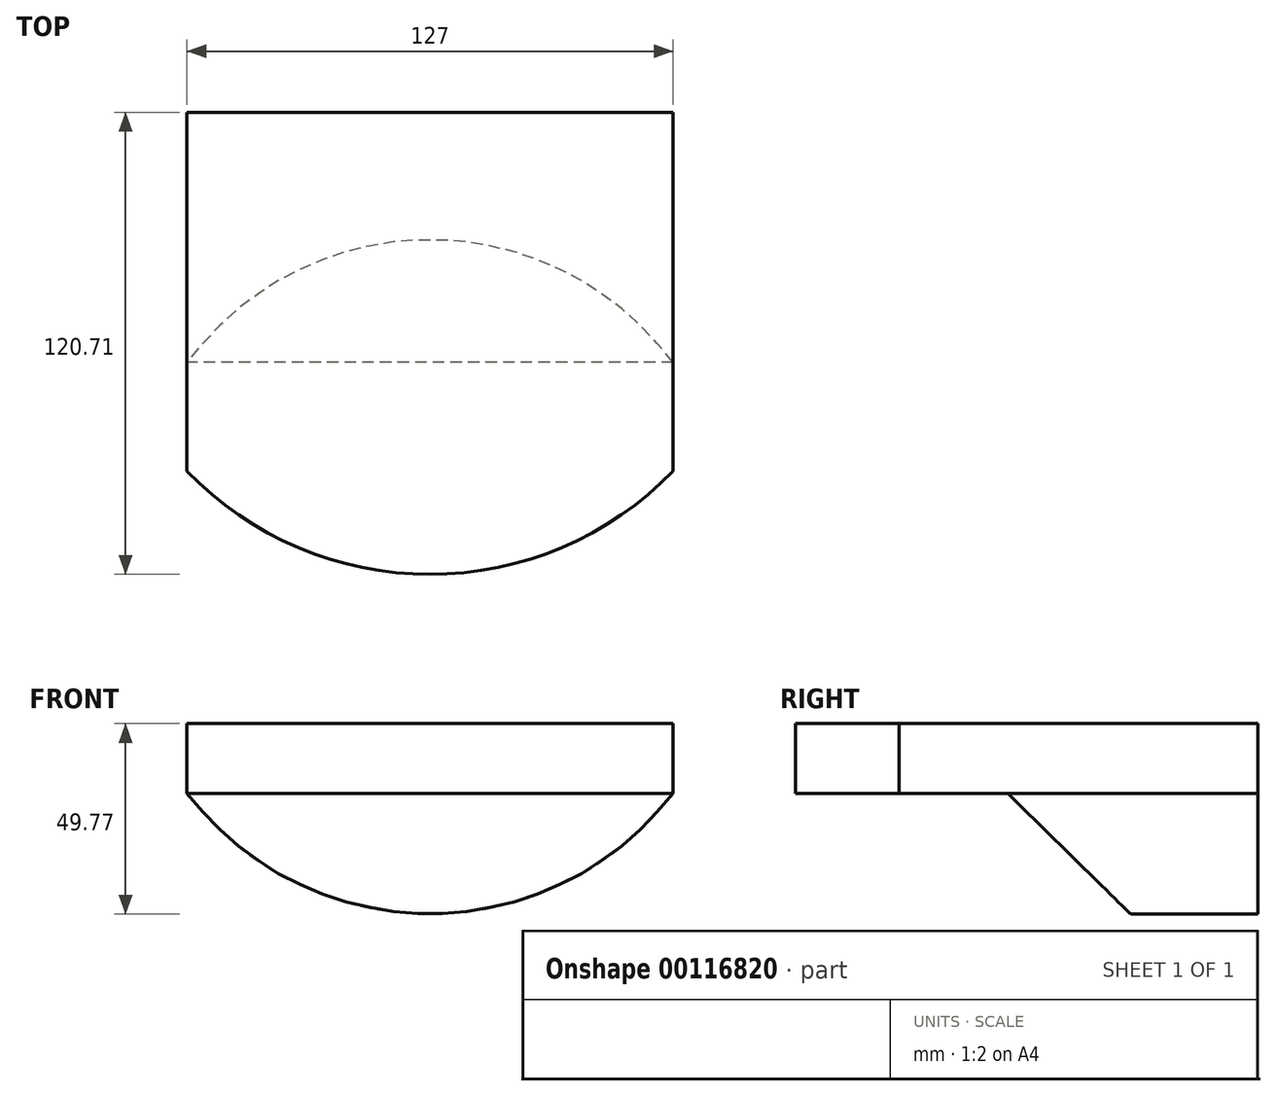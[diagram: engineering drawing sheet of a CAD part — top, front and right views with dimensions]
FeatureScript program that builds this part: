
annotation { "Feature Type Name" : "Feature", "Feature Type Description" : "" }
export const myFeature = defineFeature(function(context is Context, id is Id, definition is map)
    precondition{}
    {
        {
            var Q0;
            Q0=qCreatedBy(makeId("Front.planeOp"),FACE);
            var sketch = newSketch(context, id + "F0", { "sketchPlane" : qUnion([Q0])});
            skLineSegment(sketch, "E0.bottom", {"start": v(-63.5, 31) * mm, "end": v(63.5, 31) * mm});
            skLineSegment(sketch, "E0.top", {"start": v(-63.5, -31) * mm, "end": v(63.5, -31) * mm});
            skLineSegment(sketch, "E0.left", {"start": v(-63.5, 31) * mm, "end": v(-63.5, -31) * mm});
            skLineSegment(sketch, "E0.right", {"start": v(63.5, 31) * mm, "end": v(63.5, -31) * mm});
            skPoint(sketch, "E0.middle", {"position": v(0, 0) * mm});
            skLineSegment(sketch, "E1", {"start": v(0, 0) * mm, "end": v(0, -62.5) * mm});
            skLineSegment(sketch, "E2", {"start": v(0, -62.5) * mm, "end": v(0, 0) * mm});
            skLineSegment(sketch, "E3", {"start": v(0, 0) * mm, "end": v(0, 62.5) * mm});
            skLineSegment(sketch, "E4", {"start": v(0, 62.5) * mm, "end": v(0, 0) * mm});
            skArc(sketch, "E5", {"start": v(63.5, 31) * mm, "mid": v(0, 62.5) * mm, "end": v(-63.5, 31) * mm});
            skArc(sketch, "E6", {"start": v(-63.5, -31) * mm, "mid": v(0, -62.5) * mm, "end": v(63.5, -31) * mm});
            skSolve(sketch);
        }
        {
            var Q0;
            Q0=qSketchRegion(id+"F0",true);
            extrude(context, id + "F1", {"entities" : qUnion([Q0]), "depth" : 104.5 * mm});
        }
        {
            var Q0;
            Q0=makeQuery(id+"F1.opExtrude","SWEPT_FACE",FACE,{"disambiguationData":[OSD([sQuery(id+"F0.wireOp",EDGE,"E0.right")])]});
            var sketch = newSketch(context, id + "F2", { "sketchPlane" : qUnion([Q0])});
            skLineSegment(sketch, "E7.bottom", {"start": v(-104.5, 31) * mm, "end": v(-62.5, 31) * mm});
            skLineSegment(sketch, "E7.top", {"start": v(-104.5, -31) * mm, "end": v(-62.5, -31) * mm});
            skLineSegment(sketch, "E7.left", {"start": v(-104.5, 31) * mm, "end": v(-104.5, -31) * mm});
            skLineSegment(sketch, "E7.right", {"start": v(-62.5, 31) * mm, "end": v(-62.5, -31) * mm});
            skLineSegment(sketch, "E8", {"start": v(-62.5, 31) * mm, "end": v(-62.5, 64.33) * mm});
            skLineSegment(sketch, "E9", {"start": v(-62.5, 64.33) * mm, "end": v(-104.5, 31) * mm});
            skLineSegment(sketch, "E10", {"start": v(-62.5, -31) * mm, "end": v(-62.5, -65.1) * mm});
            skLineSegment(sketch, "E11", {"start": v(-62.5, -65.1) * mm, "end": v(-104.5, -31) * mm});
            skLineSegment(sketch, "E12", {"start": v(-104.5, -31) * mm, "end": v(-104.5, -67.31) * mm});
            skLineSegment(sketch, "E13", {"start": v(-104.5, -67.31) * mm, "end": v(-62.5, -65.1) * mm});
            skLineSegment(sketch, "E14", {"start": v(-104.5, 31) * mm, "end": v(-104.5, 72.84) * mm});
            skLineSegment(sketch, "E15", {"start": v(-104.5, 72.84) * mm, "end": v(-62.5, 64.33) * mm});
            skSolve(sketch);
        }
        {
            var Q0;
            Q0=makeQuery(id+"F2.imprint","IMPRINT",FACE,{"disambiguationData":[TD([[makeQuery(id+"F2.imprint","IMPRINT",EDGE,{"derivedFrom":sQuery(id+"F2.wireOp",EDGE,"E9")}),-1.0]])]});
            var Q1;
            Q1=makeQuery(id+"F2.imprint","IMPRINT",FACE,{"disambiguationData":[TD([[makeQuery(id+"F2.imprint","IMPRINT",EDGE,{"derivedFrom":sQuery(id+"F2.wireOp",EDGE,"E11")}),1.0]])]});
            extrude(context, id + "F3", {"entities" : qUnion([Q0, Q1]), "operationType" : NewBodyOperationType.REMOVE, "endBound" : BoundingType.THROUGH_ALL, "oppositeDirection" : true, "depth" : 25.4 * mm});
        }
        {
            var Q0;
            Q0=makeQuery(id+"F1.opExtrude","CAP_FACE",FACE,{"disambiguationData":[OSD([sQuery(id+"F0.wireOp",EDGE,"E0.left"),sQuery(id+"F0.wireOp",EDGE,"E0.right"),sQuery(id+"F0.wireOp",EDGE,"E5"),sQuery(id+"F0.wireOp",EDGE,"E6")])],"isStart":false});
            var sketch = newSketch(context, id + "F4", { "sketchPlane" : qUnion([Q0])});
            skLineSegment(sketch, "E16.bottom", {"start": v(-63.5, 31) * mm, "end": v(63.5, 31) * mm});
            skLineSegment(sketch, "E16.top", {"start": v(-63.5, -31) * mm, "end": v(63.5, -31) * mm});
            skLineSegment(sketch, "E16.left", {"start": v(-63.5, 31) * mm, "end": v(-63.5, -31) * mm});
            skLineSegment(sketch, "E16.right", {"start": v(63.5, 31) * mm, "end": v(63.5, -31) * mm});
            skSolve(sketch);
        }
        {
            var Q0;
            Q0=qSketchRegion(id+"F4",true);
            extrude(context, id + "F5", {"entities" : qUnion([Q0]), "operationType" : NewBodyOperationType.ADD, "depth" : 27 * mm});
        }
        {
            var Q0;
            Q0=makeQuery(id+"F5.opExtrude","SWEPT_FACE",FACE,{"disambiguationData":[OSD([sQuery(id+"F4.wireOp",EDGE,"E16.top")])]});
            var sketch = newSketch(context, id + "F6", { "sketchPlane" : qUnion([Q0])});
            skPoint(sketch, "E17", {"position": v(0, 131.5) * mm});
            skArc(sketch, "E18", {"start": v(63.5, 104.5) * mm, "mid": v(0, 131.5) * mm, "end": v(-63.5, 104.5) * mm});
            skLineSegment(sketch, "E19.bottom", {"start": v(-63.5, 131.5) * mm, "end": v(63.5, 131.5) * mm});
            skLineSegment(sketch, "E19.top", {"start": v(-63.5, 104.5) * mm, "end": v(63.5, 104.5) * mm});
            skLineSegment(sketch, "E19.left", {"start": v(-63.5, 131.5) * mm, "end": v(-63.5, 104.5) * mm});
            skLineSegment(sketch, "E19.right", {"start": v(63.5, 131.5) * mm, "end": v(63.5, 104.5) * mm});
            skSolve(sketch);
        }
        {
            var Q0;
            {var subQ0=sQuery(id+"F6.wireOp",EDGE,"E19.left");Q0=makeQuery(id+"F6.imprint","IMPRINT",FACE,{"disambiguationData":[TD([[makeQuery(id+"F6.imprint","IMPRINT",EDGE,{"derivedFrom":subQ0}),1.0]])]});}
            var Q1;
            {var subQ0=sQuery(id+"F6.wireOp",EDGE,"E19.right");Q1=makeQuery(id+"F6.imprint","IMPRINT",FACE,{"disambiguationData":[TD([[makeQuery(id+"F6.imprint","IMPRINT",EDGE,{"derivedFrom":subQ0}),-1.0]])]});}
            extrude(context, id + "F7", {"entities" : qUnion([Q0, Q1]), "operationType" : NewBodyOperationType.REMOVE, "endBound" : BoundingType.THROUGH_ALL, "oppositeDirection" : true, "depth" : 25.4 * mm});
        }
        {
            var Q0;
            Q0=makeQuery(id+"F1.opExtrude","CAP_FACE",FACE,{"disambiguationData":[OSD([sQuery(id+"F0.wireOp",EDGE,"E0.left"),sQuery(id+"F0.wireOp",EDGE,"E0.right"),sQuery(id+"F0.wireOp",EDGE,"E5"),sQuery(id+"F0.wireOp",EDGE,"E6")])],"isStart":true});
            var sketch = newSketch(context, id + "F8", { "sketchPlane" : qUnion([Q0])});
            skLineSegment(sketch, "E20.bottom", {"start": v(149.23, -135.48) * mm, "end": v(-88.37, -135.48) * mm});
            skLineSegment(sketch, "E20.top", {"start": v(149.23, 77.12) * mm, "end": v(-88.37, 77.12) * mm});
            skLineSegment(sketch, "E20.left", {"start": v(149.23, -135.48) * mm, "end": v(149.23, 77.12) * mm});
            skLineSegment(sketch, "E20.right", {"start": v(-88.37, -135.48) * mm, "end": v(-88.37, 77.12) * mm});
            skSolve(sketch);
        }
        {
            var Q0;
            Q0 = qSketchRegion(id + "F8", true);
            extrude(context, id + "F9", {"entities" : qUnion([Q0]), "operationType" : NewBodyOperationType.REMOVE, "oppositeDirection" : true, "depth" : 64.76 * mm});
        }
        {
            var Q0;
            Q0=makeQuery(id+"F5.boolean.opBoolean","MERGE",FACE,{"derivedFrom":[makeQuery(id+"F1.opExtrude","SWEPT_FACE",FACE,{"disambiguationData":[OSD([sQuery(id+"F0.wireOp",EDGE,"E0.right")])]}),makeQuery(id+"F5.opExtrude","SWEPT_FACE",FACE,{"disambiguationData":[OSD([sQuery(id+"F4.wireOp",EDGE,"E16.right")])]})]});
            var sketch = newSketch(context, id + "F10", { "sketchPlane" : qUnion([Q0])});
            skPoint(sketch, "E21", {"position": v(-64.76, 0) * mm});
            skPoint(sketch, "E22", {"position": v(-104.5, 0) * mm});
            skLineSegment(sketch, "E23", {"start": v(-64.76, 0) * mm, "end": v(-64.76, 76.2) * mm});
            skLineSegment(sketch, "E24", {"start": v(-64.76, 76.2) * mm, "end": v(-64.76, 0) * mm});
            skLineSegment(sketch, "E25", {"start": v(-64.76, 0) * mm, "end": v(-64.76, -12.73) * mm});
            skLineSegment(sketch, "E26", {"start": v(-64.76, -12.73) * mm, "end": v(-64.76, 0) * mm});
            skLineSegment(sketch, "E27.bottom", {"start": v(-64.76, -12.73) * mm, "end": v(-148.14, -12.73) * mm});
            skLineSegment(sketch, "E27.top", {"start": v(-64.76, 76.2) * mm, "end": v(-148.14, 76.2) * mm});
            skLineSegment(sketch, "E27.left", {"start": v(-64.76, -12.73) * mm, "end": v(-64.76, 76.2) * mm});
            skLineSegment(sketch, "E27.right", {"start": v(-148.14, -12.73) * mm, "end": v(-148.14, 76.2) * mm});
            skSolve(sketch);
        }
        {
            var Q0;
            Q0 = qSketchRegion(id + "F10", true);
            extrude(context, id + "F11", {"entities" : qUnion([Q0]), "operationType" : NewBodyOperationType.REMOVE, "endBound" : BoundingType.THROUGH_ALL, "oppositeDirection" : true, "depth" : 25.4 * mm});
        }
        {
            var Q0;
            Q0=makeQuery(id+"F9.boolean.opBoolean","COPY",FACE,{"derivedFrom":makeQuery(id+"F9.opExtrude","CAP_FACE",FACE,{"disambiguationData":[OSD([sQuery(id+"F8.wireOp",EDGE,"E20.bottom"),sQuery(id+"F8.wireOp",EDGE,"E20.top"),sQuery(id+"F8.wireOp",EDGE,"E20.left"),sQuery(id+"F8.wireOp",EDGE,"E20.right")])],"isStart":false})});
            extrude(context, id + "F12", {"entities" : qUnion([Q0]), "operationType" : NewBodyOperationType.ADD, "depth" : 25.4 * mm});
        }
        {
            var Q0;
            Q0=makeQuery(id+"F12.opExtrude","CAP_FACE",FACE,{"disambiguationData":[OSD([sQuery(id+"F8.wireOp",EDGE,"E20.bottom"),sQuery(id+"F8.wireOp",EDGE,"E20.top"),sQuery(id+"F8.wireOp",EDGE,"E20.left"),sQuery(id+"F8.wireOp",EDGE,"E20.right")])],"isStart":false});
            var sketch = newSketch(context, id + "F13", { "sketchPlane" : qUnion([Q0])});
            skLineSegment(sketch, "E28.bottom", {"start": v(63.5, -31) * mm, "end": v(-63.5, -31) * mm});
            skLineSegment(sketch, "E28.top", {"start": v(63.5, -12.73) * mm, "end": v(-63.5, -12.73) * mm});
            skLineSegment(sketch, "E28.left", {"start": v(63.5, -31) * mm, "end": v(63.5, -12.73) * mm});
            skLineSegment(sketch, "E28.right", {"start": v(-63.5, -31) * mm, "end": v(-63.5, -12.73) * mm});
            skPoint(sketch, "E29", {"position": v(0, -62.5) * mm});
            skArc(sketch, "E30", {"start": v(-63.5, -31) * mm, "mid": v(0, -62.5) * mm, "end": v(63.5, -31) * mm});
            skSolve(sketch);
        }
        {
            var Q0;
            Q0 = qSketchRegion(id + "F13", true);
            extrude(context, id + "F14", {"entities" : qUnion([Q0]), "operationType" : NewBodyOperationType.ADD, "depth" : 28.57 * mm});
        }
        {
            var Q0;
            {var subQ0=sQuery(id+"F4.wireOp",EDGE,"E16.left");var subQ1=sQuery(id+"F0.wireOp",EDGE,"E0.left");Q0=makeQuery(id+"F14.boolean.opBoolean","MERGE",FACE,{"derivedFrom":[makeQuery(id+"F12.boolean.opBoolean","MERGE",FACE,{"derivedFrom":[makeQuery(id+"F5.boolean.opBoolean","MERGE",FACE,{"derivedFrom":[makeQuery(id+"F1.opExtrude","SWEPT_FACE",FACE,{"disambiguationData":[OSD([subQ1])]}),makeQuery(id+"F5.opExtrude","SWEPT_FACE",FACE,{"disambiguationData":[OSD([subQ0])]})]}),makeQuery(id+"F12.opExtrude","SWEPT_FACE",FACE,{"disambiguationData":[OSD([subQ1,subQ0,sQuery(id+"F8.wireOp",EDGE,"E20.bottom"),sQuery(id+"F8.wireOp",EDGE,"E20.top"),sQuery(id+"F8.wireOp",EDGE,"E20.left"),sQuery(id+"F8.wireOp",EDGE,"E20.right")])]})]}),makeQuery(id+"F14.opExtrude","SWEPT_FACE",FACE,{"disambiguationData":[OSD([sQuery(id+"F13.wireOp",EDGE,"E28.left")])]})]});}
            var sketch = newSketch(context, id + "F15", { "sketchPlane" : qUnion([Q0])});
            skLineSegment(sketch, "E31", {"start": v(104.5, -31) * mm, "end": v(76.03, -31) * mm});
            skLineSegment(sketch, "E32", {"start": v(76.03, -31) * mm, "end": v(104.5, -31) * mm});
            skLineSegment(sketch, "E33", {"start": v(76.03, -31) * mm, "end": v(42.23, -64.2) * mm});
            skLineSegment(sketch, "E34", {"start": v(42.23, -64.2) * mm, "end": v(104.03, -67.29) * mm});
            skLineSegment(sketch, "E35", {"start": v(104.03, -67.29) * mm, "end": v(104.5, -31) * mm});
            skSolve(sketch);
        }
        {
            var Q0;
            Q0 = qSketchRegion(id + "F15", true);
            extrude(context, id + "F16", {"entities" : qUnion([Q0]), "operationType" : NewBodyOperationType.REMOVE, "endBound" : BoundingType.THROUGH_ALL, "oppositeDirection" : true, "depth" : 25.4 * mm});
        }
    });
